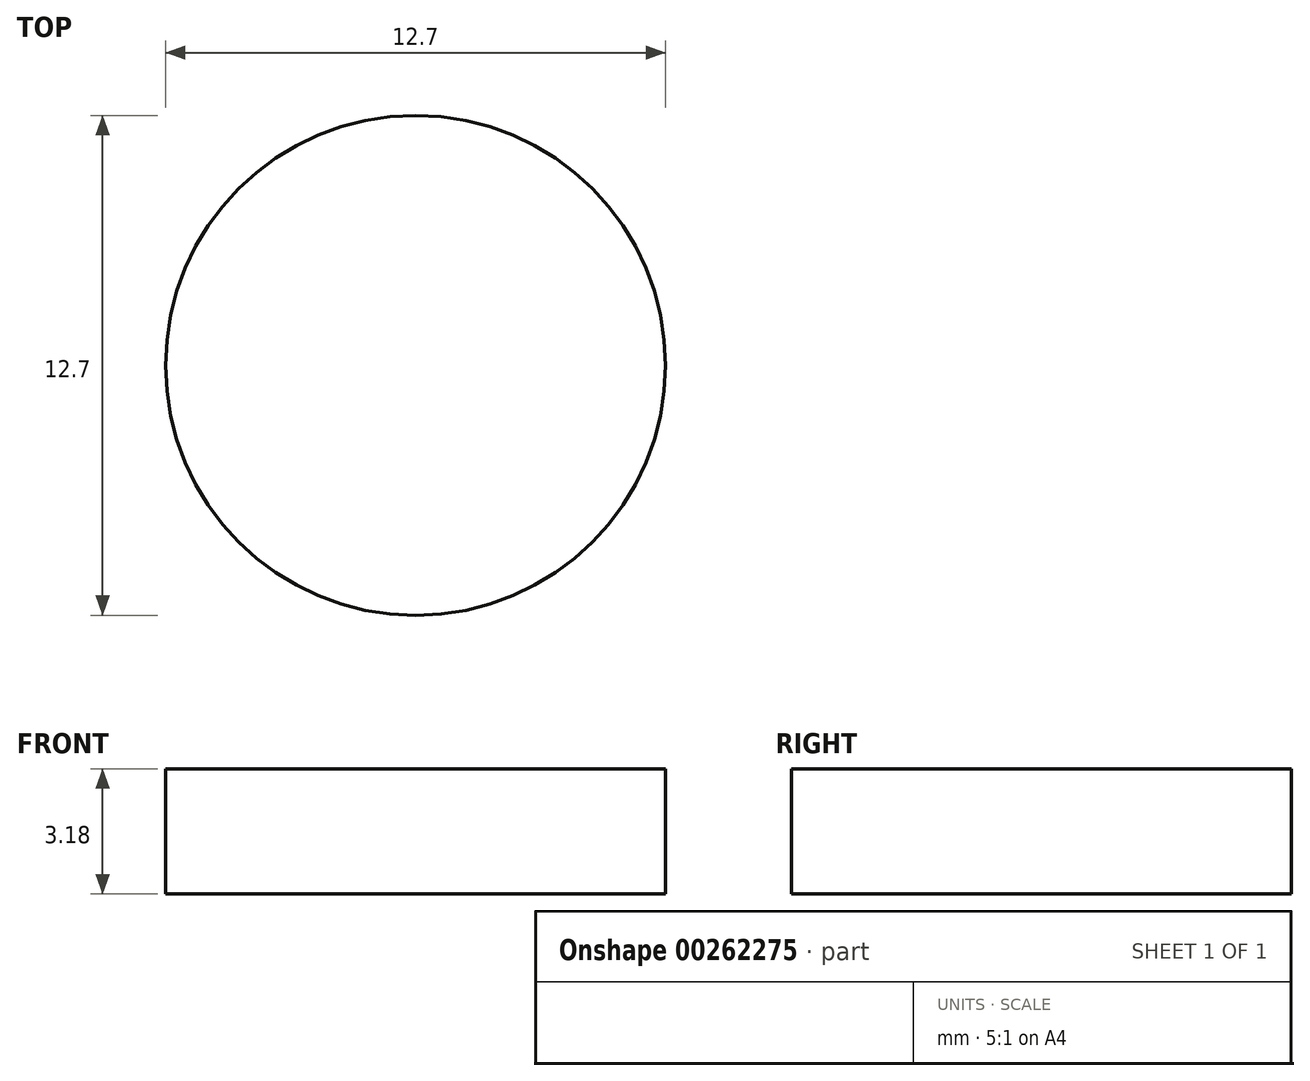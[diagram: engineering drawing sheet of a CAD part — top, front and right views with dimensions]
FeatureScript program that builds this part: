
annotation { "Feature Type Name" : "Feature", "Feature Type Description" : "" }
export const myFeature = defineFeature(function(context is Context, id is Id, definition is map)
    precondition{}
    {
        {
            var Q0;
            Q0=qCreatedBy(makeId("Top.planeOp"),FACE);
            var sketch = newSketch(context, id + "F0", { "sketchPlane" : qUnion([Q0])});
            skCircle(sketch, "E0", {"center": v(0, 0) * mm, "radius": 6.35 * mm});
            skSolve(sketch);
        }
        {
            var Q0;
            Q0=makeQuery(id+"F0.imprint","IMPRINT",FACE,{"disambiguationData":[TD([[makeQuery(id+"F0.imprint","IMPRINT",EDGE,{"derivedFrom":sQuery(id+"F0.wireOp",EDGE,"E0")}),1.0]])]});
            extrude(context, id + "F1", {"entities" : qUnion([Q0]), "depth" : 3.17 * mm});
        }
    });
